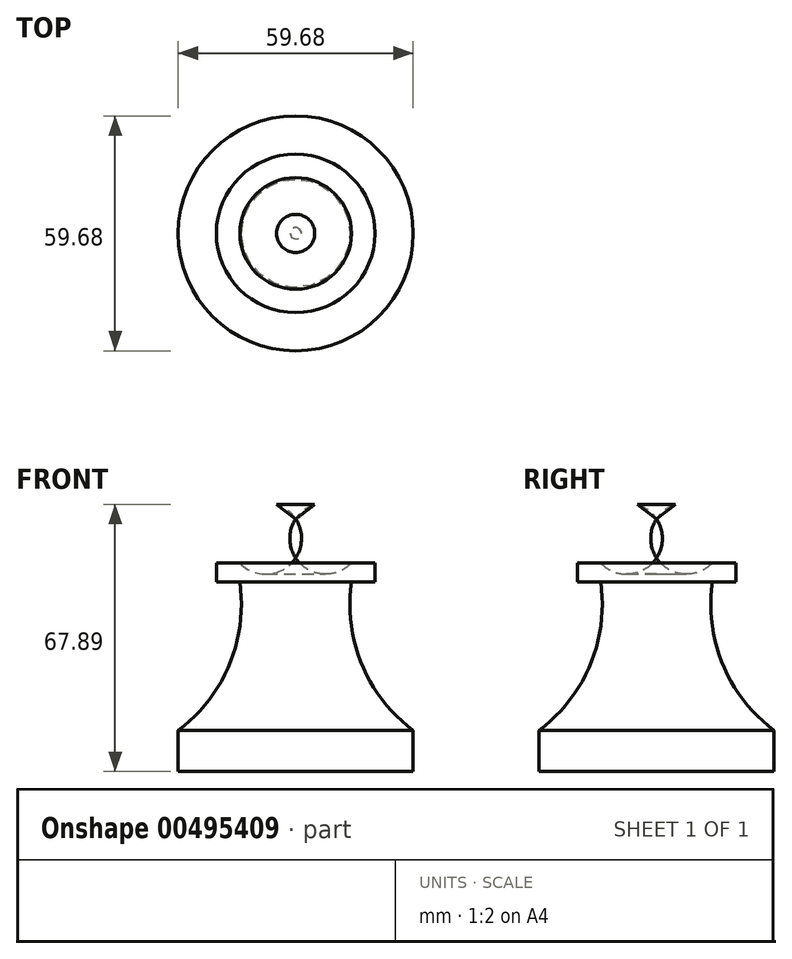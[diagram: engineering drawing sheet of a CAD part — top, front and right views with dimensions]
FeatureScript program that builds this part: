
annotation { "Feature Type Name" : "Feature", "Feature Type Description" : "" }
export const myFeature = defineFeature(function(context is Context, id is Id, definition is map)
    precondition{}
    {
        {
            var Q0;
            Q0=qCreatedBy(makeId("Right.planeOp"),FACE);
            var sketch = newSketch(context, id + "F0", { "sketchPlane" : qUnion([Q0])});
            skLineSegment(sketch, "E0", {"start": v(0, 0) * mm, "end": v(-29.84, 0) * mm});
            skLineSegment(sketch, "E1", {"start": v(-29.84, 0) * mm, "end": v(-29.84, 10.45) * mm});
            skArc(sketch, "E2", {"start": v(-29.84, 10.45) * mm, "mid": v(-16.85, 27.14) * mm, "end": v(-14.18, 48.12) * mm});
            skLineSegment(sketch, "E3", {"start": v(-14.18, 48.12) * mm, "end": v(-20.14, 48.12) * mm});
            skLineSegment(sketch, "E4", {"start": v(-20.14, 48.12) * mm, "end": v(-20.14, 52.97) * mm});
            skLineSegment(sketch, "E5", {"start": v(-20.14, 52.97) * mm, "end": v(-14.18, 52.97) * mm});
            skArc(sketch, "E6", {"start": v(-4.85, 67.9) * mm, "mid": v(-15.3, 64.05) * mm, "end": v(-14.18, 52.97) * mm});
            skLineSegment(sketch, "E7", {"start": v(0, 0) * mm, "end": v(0, 64.16) * mm});
            skLineSegment(sketch, "E8", {"start": v(0, 64.16) * mm, "end": v(-4.85, 67.9) * mm});
            skSolve(sketch);
        }
        {
            var Q0;
            Q0=makeQuery(id+"F0.imprint","IMPRINT",FACE,{"disambiguationData":[TD([[makeQuery(id+"F0.imprint","IMPRINT",EDGE,{"derivedFrom":sQuery(id+"F0.wireOp",EDGE,"E0")}),-1.0]])]});
            var Q1;
            Q1=sQuery(id+"F0.wireOp",EDGE,"E7");
            revolve(context, id + "F1", {"entities" : qUnion([Q0]), "axis" : qUnion([Q1]), "revolveType" : RevolveType.FULL});
        }
    });
